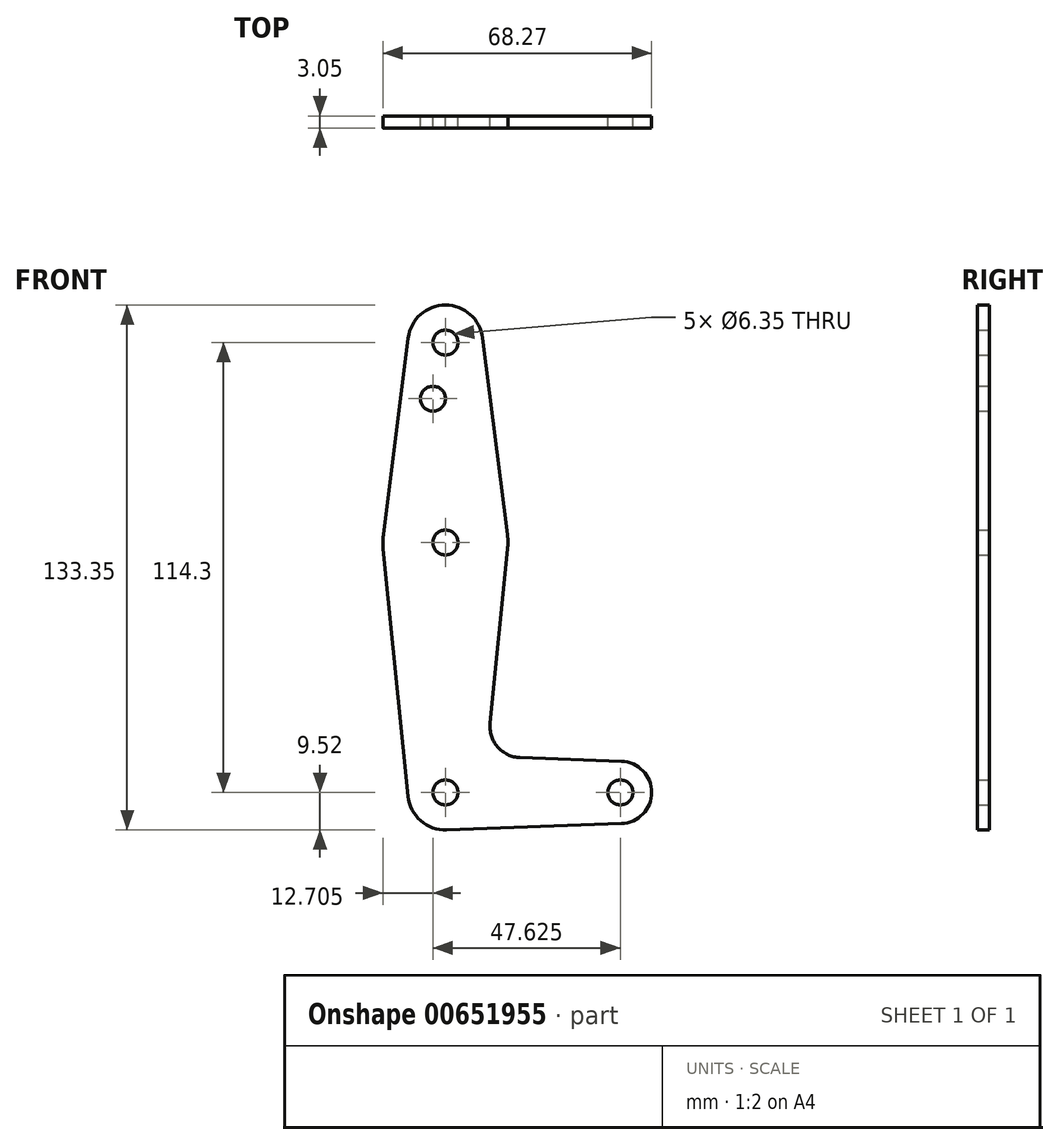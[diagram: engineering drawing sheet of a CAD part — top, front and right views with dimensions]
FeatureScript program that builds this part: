
annotation { "Feature Type Name" : "Feature", "Feature Type Description" : "" }
export const myFeature = defineFeature(function(context is Context, id is Id, definition is map)
    precondition{}
    {
        {
            var Q0;
            Q0=qCreatedBy(makeId("Front.planeOp"),FACE);
            var sketch = newSketch(context, id + "F0", { "sketchPlane" : qUnion([Q0])});
            skLineSegment(sketch, "E0", {"start": v(0, 114.3) * mm, "end": v(0, 0) * mm, "construction": true});
            skLineSegment(sketch, "E1", {"start": v(0, 0) * mm, "end": v(44.45, 0) * mm, "construction": true});
            skCircle(sketch, "E2", {"center": v(0, 63.5) * mm, "radius": 15.88 * mm});
            skCircle(sketch, "E3", {"center": v(0, 114.3) * mm, "radius": 9.53 * mm});
            skCircle(sketch, "E4", {"center": v(0, 0) * mm, "radius": 9.53 * mm});
            skCircle(sketch, "E5", {"center": v(44.45, 0) * mm, "radius": 7.94 * mm});
            skLineSegment(sketch, "E6", {"start": v(-9.45, 115.5) * mm, "end": v(-15.75, 65.48) * mm});
            skLineSegment(sketch, "E7", {"start": v(-15.8, 61.91) * mm, "end": v(-9.48, -0.95) * mm});
            skLineSegment(sketch, "E8", {"start": v(0.34, -9.52) * mm, "end": v(44.73, -7.93) * mm});
            skLineSegment(sketch, "E9", {"start": v(44.73, 7.93) * mm, "end": v(18.97, 8.85) * mm});
            skLineSegment(sketch, "E10", {"start": v(15.8, 61.91) * mm, "end": v(11.34, 17.6) * mm});
            skLineSegment(sketch, "E11", {"start": v(15.75, 65.48) * mm, "end": v(9.45, 115.5) * mm});
            skCircle(sketch, "E12", {"center": v(0, 114.3) * mm, "radius": 3.18 * mm});
            skCircle(sketch, "E13", {"center": v(0, 63.5) * mm, "radius": 3.18 * mm});
            skCircle(sketch, "E14", {"center": v(0, 0) * mm, "radius": 3.18 * mm});
            skCircle(sketch, "E15", {"center": v(44.45, 0) * mm, "radius": 3.18 * mm});
            skArc(sketch, "E16.filletArc", {"start": v(11.34, 17.6) * mm, "mid": v(13.26, 11.57) * mm, "end": v(18.97, 8.85) * mm});
            skCircle(sketch, "E17", {"center": v(-3.17, 100.03) * mm, "radius": 3.18 * mm});
            skSolve(sketch);
        }
        {
            var Q0;
            {var subQ1=sQuery(id+"F0.wireOp",EDGE,"E6");Q0=makeQuery(id+"F0.imprint","IMPRINT",FACE,{"disambiguationData":[TD([[makeQuery(id+"F0.imprint","IMPRINT",EDGE,{"derivedFrom":subQ1}),1.0]])]});}
            var Q1;
            Q1=makeQuery(id+"F0.imprint","IMPRINT",FACE,{"disambiguationData":[TD([[makeQuery(id+"F0.imprint","IMPRINT",EDGE,{"derivedFrom":sQuery(id+"F0.wireOp",EDGE,"E12")}),-1.0]])]});
            var Q2;
            {var subQ0=sQuery(id+"F0.wireOp",EDGE,"E7");Q2=makeQuery(id+"F0.imprint","IMPRINT",FACE,{"disambiguationData":[TD([[makeQuery(id+"F0.imprint","IMPRINT",EDGE,{"derivedFrom":subQ0}),1.0]])]});}
            var Q3;
            Q3=makeQuery(id+"F0.imprint","IMPRINT",FACE,{"disambiguationData":[TD([[makeQuery(id+"F0.imprint","IMPRINT",EDGE,{"derivedFrom":sQuery(id+"F0.wireOp",EDGE,"E13")}),-1.0]])]});
            var Q4;
            Q4=makeQuery(id+"F0.imprint","IMPRINT",FACE,{"disambiguationData":[TD([[makeQuery(id+"F0.imprint","IMPRINT",EDGE,{"derivedFrom":sQuery(id+"F0.wireOp",EDGE,"E14")}),-1.0]])]});
            var Q5;
            Q5=makeQuery(id+"F0.imprint","IMPRINT",FACE,{"disambiguationData":[TD([[makeQuery(id+"F0.imprint","IMPRINT",EDGE,{"derivedFrom":sQuery(id+"F0.wireOp",EDGE,"E15")}),-1.0]])]});
            extrude(context, id + "F1", {"entities" : qUnion([Q0, Q1, Q2, Q3, Q4, Q5]), "depth" : 3.05 * mm, "offsetDistance" : 25.4 * mm});
        }
    });
